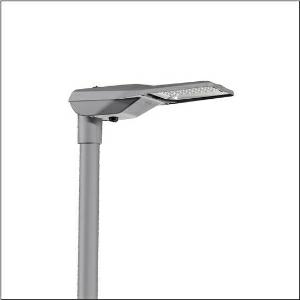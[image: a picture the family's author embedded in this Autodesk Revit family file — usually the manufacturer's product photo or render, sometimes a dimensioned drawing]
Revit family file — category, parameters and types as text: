
# Revit family: streetlight_sl_21_mini___st1_0a_5xe2d43t08hb_126b
name_source: partatom
category: Lighting Fixtures
units: mm (PartAtom-declared; Revit-internal decimal feet)

## family parameters
Cut with Voids When Loaded = No
Host = Face
Light Source = No
Part Type = Normal
Room Calculation Point = No
Round Connector Dimension = Use Diameter
Shared = No

## types (1)
- --- (1 x LED, 9430 lm, 66 W, 4000K)
    Apparent Load = 66 VA
    CIE Flux Codes = 37 72 97 100 100
    Color Rendering = 70
    Color Temperature = 4000K
    Default Elevation = 1800 mm
    Description = Streetlight SL 21 mini, mast luminaire, primary light control with lens, of PMMA, primary optical cover: cover, of toughened safety glass, transparent, light distribution: ST1.0a, light emission: direct distribution, primary light characteristic: asymmetric, installation type: side-entry, post-top, LED, High Power LED, rated luminous flux: 9.430lm, luminous efficacy: 143lm/W, light colour: 740, colour temperature: 4000K, control gear: D4i, control: overheat protection, constant luminous flux control, time-dependent luminous flux control, flexible luminous flux parameterisation, pre-setting: logarithmic dimming characteristic, mains connection: 220..240V, AC, 50/60Hz, start of lifetime: 66W, end of service life: 69W, reduction: 30W, luminaire housing, of diecast aluminium, powder-coated, Siteco® metallic grey (DB 702S), corrosivity category C5 mid according to DIN EN ISO 12944, please order mast flange separately, inclination adjustable: 0°, 5°, 10°, 15°, sealing non-destructively replaceable, multi-level sealing system, length: 628mm, width: 235mm, height: 110mm, mast flange for spigot size: 42mm (side-entry): 5XC10008XM4, 60/48mm (side-entry/post-top): 5XC10108XM2, 76/60mm (side-entry/post-top): 5XC10108XM1, mounting height: 4..8m, Smart Interface below and above, protection rating (complete): IP66, insulation class (complete): insulation class II (safety insulation), certification: CE, ENEC, ENEC+, VDE, impact resistance: IK10, permissible operating ambient temperature for outdoor applications: -40..+50°C, standard-compliant lighting for roads and squares, packaging unit: 1 piece

Light Distribution: ST1.0a
    Height = 110 mm
    Lamp = 1 x LED
    Lamp Light Flux = 9430 lm
    Lamp Power = 66 W
    Lamp count = 1
    Length = 625 mm
    Luminous efficacy = 143 lm/W
    Manufacturer = Siteco
    ModVariant = No
    Model = 5XE2D43T08HB
    Number of Poles = 1
    OnlyDefault = Yes
    Power Factor = 1
    Product Name = Streetlight SL 21 mini | ST1.0a
    Product group = mast luminaire | pylon top
    ProductGroupID = 6100
    Protection Class = Protection class II
    Protection Degree = IP 66
    RLX_Detail_Level = 1
    RLX_Emergency_Light_Flux = 0 lm
    RLX_Emergency_Type = 0
    RLX_Emergency_Type_DB = No
    RlxData = <blob elided: 26265 chars, md5=8afdaaad>
    Socket = socket
    Standby Power = 0 W
    System Light Flux = 9430 lm
    System Power = 66 W
    Type Comments = factory setting: luminous flux: 100 % | dim-lin: 254 | 670 mA
    Type Image = l_1003514.jpg
    URL = http://relux.com
    VarID = @adj_188434
    Voltage = 0 V
    Weight = 0.00 kg
    Width = 234 mm

## geometry (parser evidence)
native form markers: Blend x4, Sweep x13
no freeform markers — native parametric forms only
